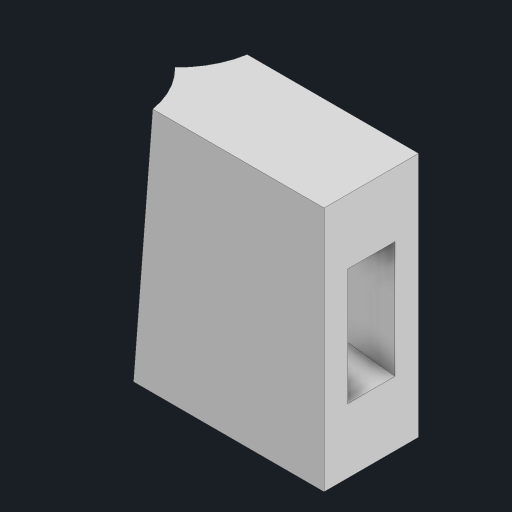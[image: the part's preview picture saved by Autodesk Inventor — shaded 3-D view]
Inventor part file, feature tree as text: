
AUTODESK INVENTOR PART (.ipt)
format: ipt  version: 2023.1 (Build 271208000, 208)  size: 153,088 bytes
history: native  units: mm
features: sketch x3, projected_geometry x2, plane x1, loft x1, extrude x1
ambient origin geometry x8: Origin, YZ Plane, XZ Plane, XY Plane, X Axis, Y Axis, Z Axis, Center Point
bodies: Body1 (feature_tree)
feature tree (8):
  sketch  "Sketch2"  dims[d0=13.0mm d2=0.5mm]
  plane  "Work Plane1"
  loft  "Loft1"
  extrude  "Extrusion2"  Depth=3.0mm
  sketch  "Sketch3"  dims[d4=0.5mm d5=3.0mm]
  sketch  "Sketch5"  dims[d6=10.0mm d8=20.0mm d9=0.5mm d11=8.0mm d16=17.0mm d17=0.5mm d18=0.0mm d19=90.0deg d20=0.0mm d21=90.0deg d26=26.0mm d27=4.401924mm d29=10.0mm d30=1.127387mm d31=1.127387mm d32=5.0mm d33=0.0mm d34=10.0mm]
  projected_geometry  "Projected Loop1"
  projected_geometry  "Projected Loop2"
